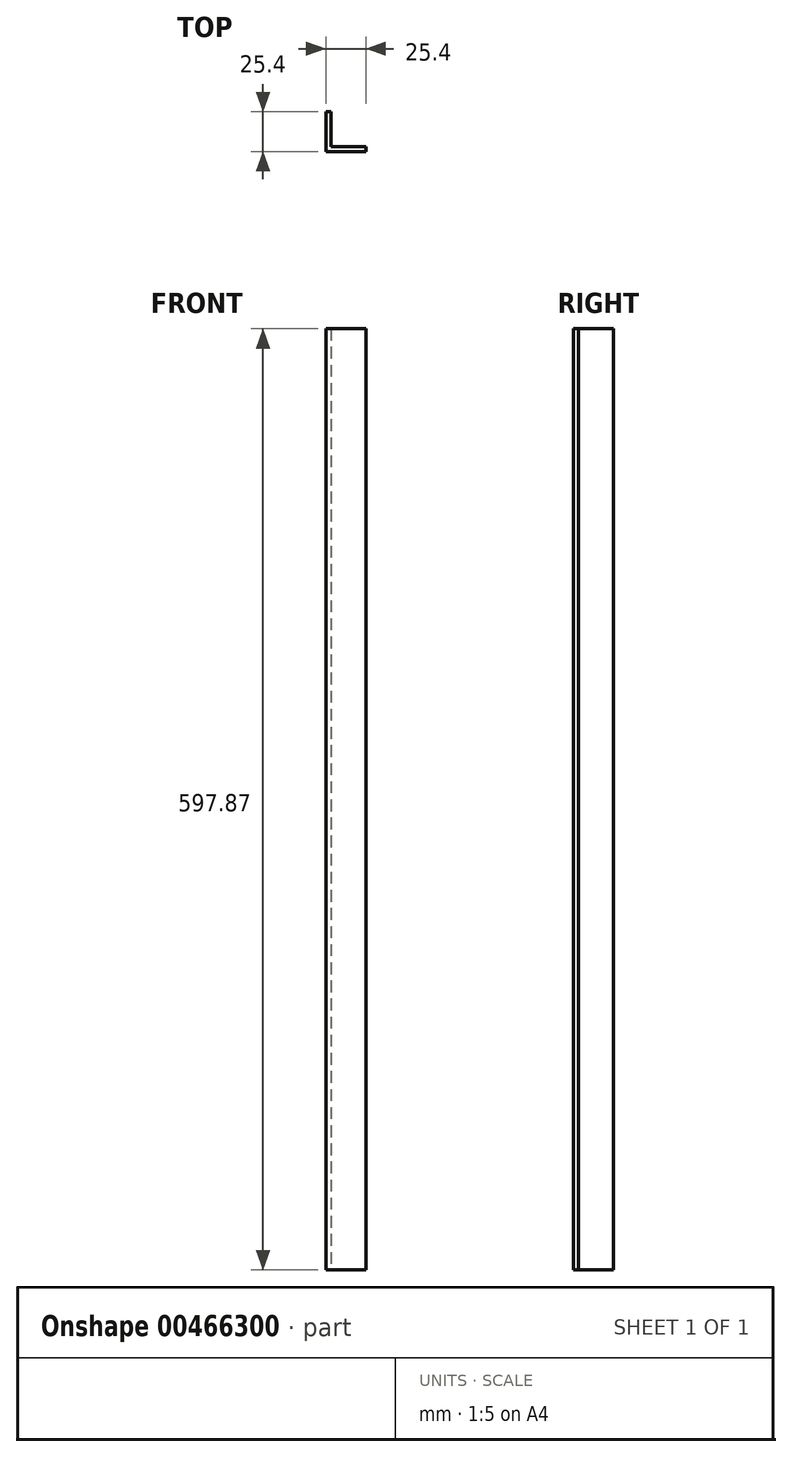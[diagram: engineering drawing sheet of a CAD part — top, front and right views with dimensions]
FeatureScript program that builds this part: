
annotation { "Feature Type Name" : "Feature", "Feature Type Description" : "" }
export const myFeature = defineFeature(function(context is Context, id is Id, definition is map)
    precondition{}
    {
        {
            var Q0;
            Q0=qCreatedBy(makeId("Top.planeOp"),FACE);
            var sketch = newSketch(context, id + "F0", { "sketchPlane" : qUnion([Q0])});
            skLineSegment(sketch, "E0", {"start": v(-53.13, 0) * mm, "end": v(-27.73, 0) * mm});
            skLineSegment(sketch, "E1", {"start": v(-27.73, 0) * mm, "end": v(-27.73, 3.18) * mm});
            skLineSegment(sketch, "E2", {"start": v(-27.73, 3.18) * mm, "end": v(-49.95, 3.17) * mm});
            skLineSegment(sketch, "E3", {"start": v(-49.95, 3.17) * mm, "end": v(-49.95, 25.4) * mm});
            skLineSegment(sketch, "E4", {"start": v(-49.95, 25.4) * mm, "end": v(-53.13, 25.4) * mm});
            skLineSegment(sketch, "E5", {"start": v(-53.13, 25.4) * mm, "end": v(-53.13, 0) * mm});
            skSolve(sketch);
        }
        {
            var Q0;
            Q0=makeQuery(id+"F0.imprint","IMPRINT",FACE,{"disambiguationData":[TD([[makeQuery(id+"F0.imprint","IMPRINT",EDGE,{"derivedFrom":sQuery(id+"F0.wireOp",EDGE,"E0")}),1.0]])]});
            extrude(context, id + "F1", {"entities" : qUnion([Q0]), "depth" : 597.87 * mm});
        }
    });
